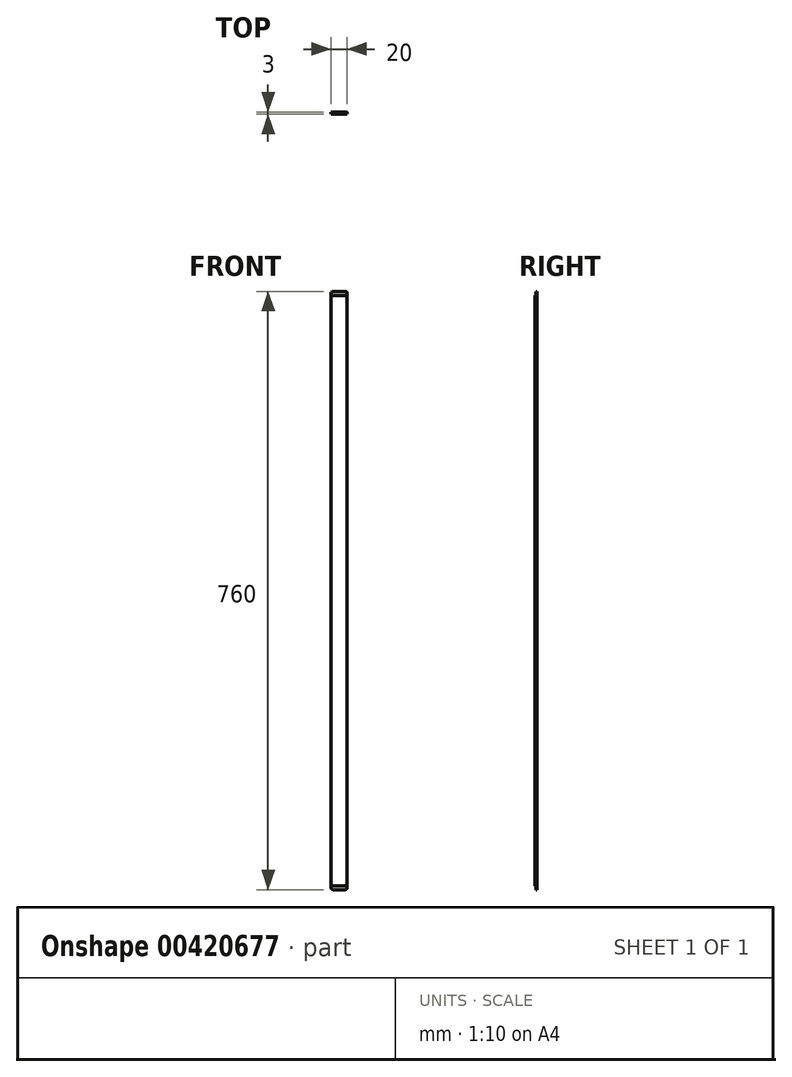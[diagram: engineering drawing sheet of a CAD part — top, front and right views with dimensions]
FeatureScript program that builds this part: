
annotation { "Feature Type Name" : "Feature", "Feature Type Description" : "" }
export const myFeature = defineFeature(function(context is Context, id is Id, definition is map)
    precondition{}
    {
        {
            var Q0;
            Q0=qCreatedBy(makeId("Front.planeOp"),FACE);
            var sketch = newSketch(context, id + "F0", { "sketchPlane" : qUnion([Q0])});
            skLineSegment(sketch, "E0.bottom", {"start": v(10, -380) * mm, "end": v(-10, -380) * mm});
            skLineSegment(sketch, "E0.top", {"start": v(10, 380) * mm, "end": v(-10, 380) * mm});
            skLineSegment(sketch, "E0.left", {"start": v(10, -380) * mm, "end": v(10, 380) * mm});
            skLineSegment(sketch, "E0.right", {"start": v(-10, -380) * mm, "end": v(-10, 380) * mm});
            skPoint(sketch, "E0.middle", {"position": v(0, 0) * mm});
            skSolve(sketch);
        }
        {
            var Q0;
            Q0=qSketchRegion(id+"F0",true);
            extrude(context, id + "F1", {"entities" : qUnion([Q0]), "depth" : 3 * mm});
        }
        {
            var Q0;
            Q0=makeQuery(id+"F1.opExtrude","CAP_FACE",FACE,{"disambiguationData":[OSD([sQuery(id+"F0.wireOp",EDGE,"E0.bottom"),sQuery(id+"F0.wireOp",EDGE,"E0.top"),sQuery(id+"F0.wireOp",EDGE,"E0.left"),sQuery(id+"F0.wireOp",EDGE,"E0.right")])],"isStart":false});
            var sketch = newSketch(context, id + "F2", { "sketchPlane" : qUnion([Q0])});
            skLineSegment(sketch, "E1", {"start": v(-10, 380) * mm, "end": v(10, 380) * mm});
            skLineSegment(sketch, "E2", {"start": v(10, 380) * mm, "end": v(10, 375) * mm});
            skLineSegment(sketch, "E3", {"start": v(10, 375) * mm, "end": v(-10, 375) * mm});
            skLineSegment(sketch, "E4", {"start": v(-10, 375) * mm, "end": v(-10, 380) * mm});
            skLineSegment(sketch, "E5", {"start": v(-10, -380) * mm, "end": v(10, -380) * mm});
            skLineSegment(sketch, "E6", {"start": v(10, -380) * mm, "end": v(10, -375) * mm});
            skLineSegment(sketch, "E7", {"start": v(10, -375) * mm, "end": v(-10, -375) * mm});
            skLineSegment(sketch, "E8", {"start": v(-10, -375) * mm, "end": v(-10, -380) * mm});
            skSolve(sketch);
        }
        {
            var Q0;
            Q0=makeQuery(id+"F2.imprint","IMPRINT",FACE,{"disambiguationData":[TD([[makeQuery(id+"F2.imprint","IMPRINT",EDGE,{"derivedFrom":sQuery(id+"F2.wireOp",EDGE,"E1")}),1.0]])]});
            var Q1;
            Q1=makeQuery(id+"F2.imprint","IMPRINT",FACE,{"disambiguationData":[TD([[makeQuery(id+"F2.imprint","IMPRINT",EDGE,{"derivedFrom":sQuery(id+"F2.wireOp",EDGE,"E5")}),-1.0]])]});
            extrude(context, id + "F3", {"entities" : qUnion([Q0, Q1]), "operationType" : NewBodyOperationType.REMOVE, "oppositeDirection" : true, "depth" : 1.5 * mm});
        }
        {
            var Q0;
            Q0=makeQuery(id+"F1.opExtrude","SWEPT_EDGE",EDGE,{"disambiguationData":[OSD([sQuery(id+"F0.wireOp",EDGE,"E0.bottom"),sQuery(id+"F0.wireOp",EDGE,"E0.left")])]});
            var Q1;
            Q1=makeQuery(id+"F1.opExtrude","SWEPT_EDGE",EDGE,{"disambiguationData":[OSD([sQuery(id+"F0.wireOp",EDGE,"E0.bottom"),sQuery(id+"F0.wireOp",EDGE,"E0.right")])]});
            var Q2;
            Q2=makeQuery(id+"F1.opExtrude","SWEPT_EDGE",EDGE,{"disambiguationData":[OSD([sQuery(id+"F0.wireOp",EDGE,"E0.top"),sQuery(id+"F0.wireOp",EDGE,"E0.right")])]});
            var Q3;
            Q3=makeQuery(id+"F1.opExtrude","SWEPT_EDGE",EDGE,{"disambiguationData":[OSD([sQuery(id+"F0.wireOp",EDGE,"E0.top"),sQuery(id+"F0.wireOp",EDGE,"E0.left")])]});
            fillet(context, id + "F4", {"entities" : qUnion([Q0, Q1, Q2, Q3]), "radius" : 2 * mm, "tangentPropagation" : true, "allowEdgeOverflow" : false});
        }
    });
